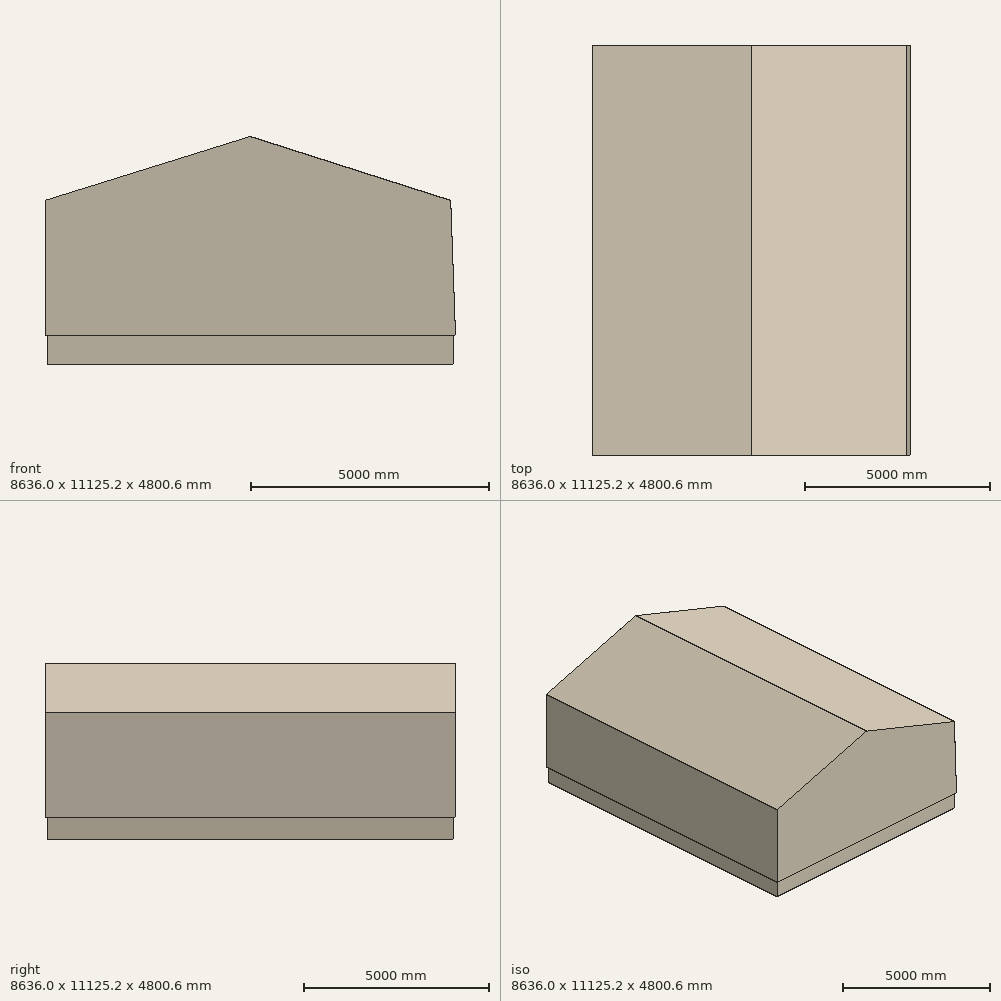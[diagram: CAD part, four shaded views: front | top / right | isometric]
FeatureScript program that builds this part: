
annotation { "Feature Type Name" : "Feature", "Feature Type Description" : "" }
export const myFeature = defineFeature(function(context is Context, id is Id, definition is map)
    precondition{}
    {
        {
            var Q0;
            Q0=qCreatedBy(makeId("Front.planeOp"),FACE);
            var sketch = newSketch(context, id + "F0", { "sketchPlane" : qUnion([Q0])});
            skLineSegment(sketch, "E0.0", {"start": v(-1530.49, 55.35) * mm, "end": v(7105.51, 55.35) * mm});
            skLineSegment(sketch, "E1", {"start": v(-1530.49, 2900.15) * mm, "end": v(-1530.49, 55.35) * mm});
            skLineSegment(sketch, "E2", {"start": v(7003.91, 2900.15) * mm, "end": v(7105.51, 55.35) * mm});
            skLineSegment(sketch, "E3", {"start": v(2787.51, 55.35) * mm, "end": v(2787.51, 4246.35) * mm, "construction": true});
            skLineSegment(sketch, "E4", {"start": v(2787.51, 4246.35) * mm, "end": v(7003.91, 2900.15) * mm});
            skLineSegment(sketch, "E5", {"start": v(2787.51, 4246.35) * mm, "end": v(-1530.49, 2900.15) * mm});
            skSolve(sketch);
        }
        {
            var Q0;
            Q0=makeQuery(id+"F0.imprint","IMPRINT",FACE,{"disambiguationData":[TD([[makeQuery(id+"F0.imprint","IMPRINT",EDGE,{"derivedFrom":sQuery(id+"F0.wireOp",EDGE,"E0.0")}),1.0]])]});
            extrude(context, id + "F1", {"entities" : qUnion([Q0]), "depth" : 11125.2 * mm, "offsetDistance" : 30.48 * mm});
        }
        {
            var Q0;
            Q0=makeQuery(id+"F1.opExtrude","SWEPT_FACE",FACE,{"disambiguationData":[OSD([sQuery(id+"F0.wireOp",EDGE,"E0.0")])]});
            var sketch = newSketch(context, id + "F2", { "sketchPlane" : qUnion([Q0])});
            skLineSegment(sketch, "E6.0", {"start": v(-1479.69, 50.8) * mm, "end": v(7054.71, 50.8) * mm});
            skLineSegment(sketch, "E6.1", {"start": v(-1479.69, 11074.4) * mm, "end": v(-1479.69, 50.8) * mm});
            skLineSegment(sketch, "E6.2", {"start": v(7054.71, 11074.4) * mm, "end": v(-1479.69, 11074.4) * mm});
            skLineSegment(sketch, "E6.3", {"start": v(7054.71, 50.8) * mm, "end": v(7054.71, 11074.4) * mm});
            skSolve(sketch);
        }
        {
            var Q0;
            Q0=makeQuery(id+"F2.imprint","IMPRINT",FACE,{"disambiguationData":[TD([[makeQuery(id+"F2.imprint","IMPRINT",EDGE,{"derivedFrom":sQuery(id+"F2.wireOp",EDGE,"E6.0")}),1.0]])]});
            extrude(context, id + "F3", {"entities" : qUnion([Q0]), "operationType" : NewBodyOperationType.ADD, "depth" : 609.6 * mm, "offsetDistance" : 30.48 * mm});
        }
    });
